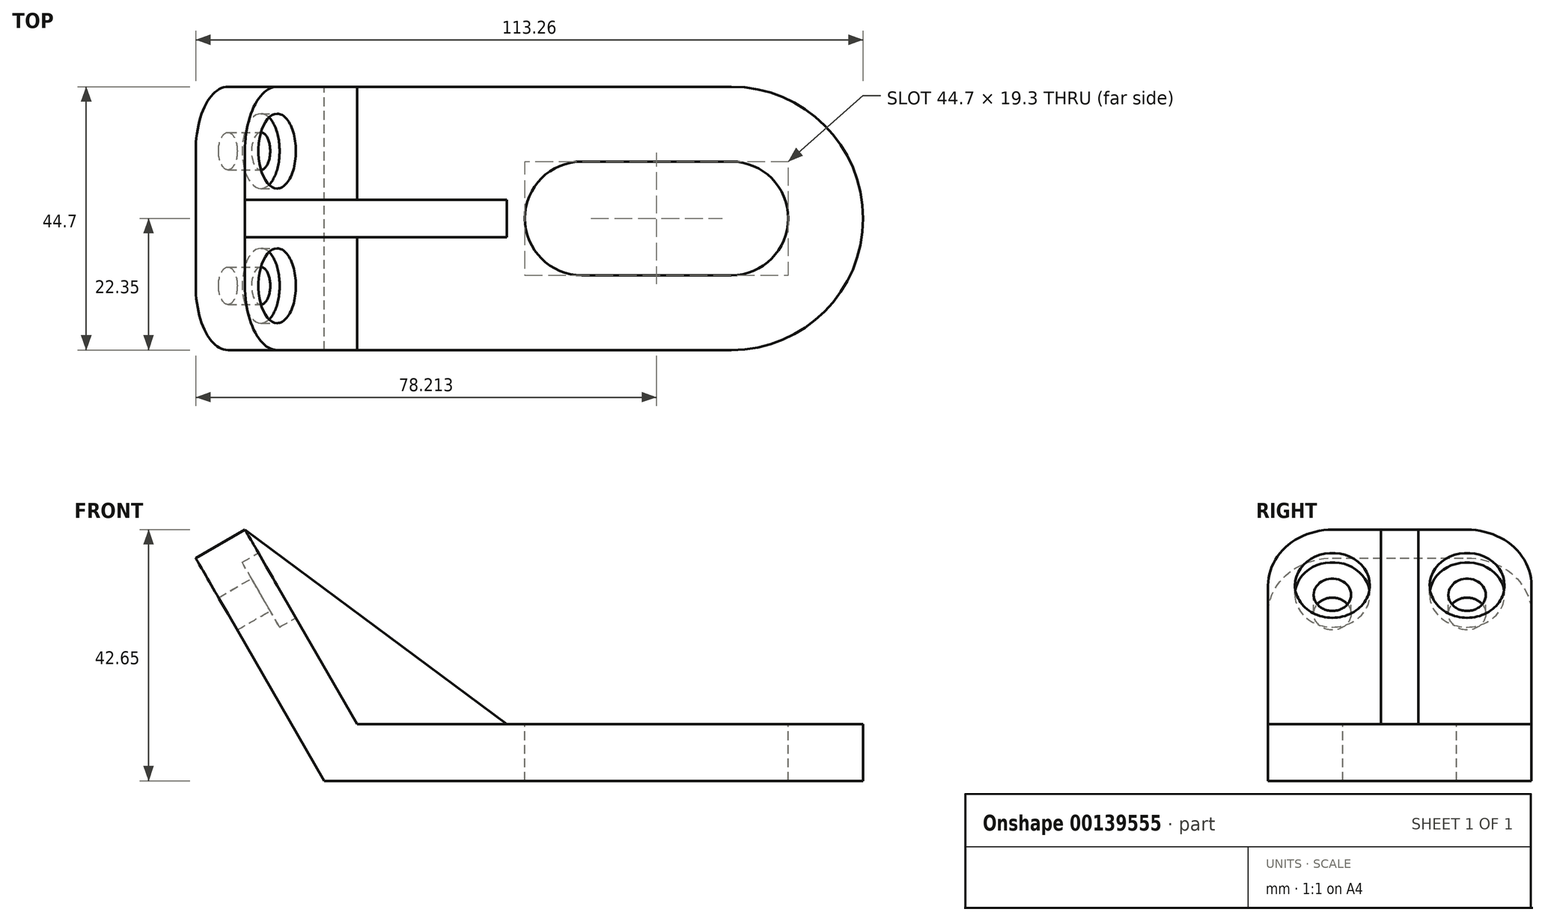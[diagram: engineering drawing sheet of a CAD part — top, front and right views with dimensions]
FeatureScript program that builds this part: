
annotation { "Feature Type Name" : "Feature", "Feature Type Description" : "" }
export const myFeature = defineFeature(function(context is Context, id is Id, definition is map)
    precondition{}
    {
        {
            var Q0;
            Q0=qCreatedBy(makeId("Front.planeOp"),FACE);
            var sketch = newSketch(context, id + "F0", { "sketchPlane" : qUnion([Q0])});
            skLineSegment(sketch, "E0", {"start": v(0, 0) * mm, "end": v(91.42, 0) * mm});
            skLineSegment(sketch, "E1", {"start": v(91.42, 0) * mm, "end": v(91.42, 9.65) * mm});
            skLineSegment(sketch, "E2", {"start": v(0, 0) * mm, "end": v(-21.84, 37.82) * mm});
            skLineSegment(sketch, "E3", {"start": v(-21.84, 37.82) * mm, "end": v(-13.48, 42.65) * mm});
            skLineSegment(sketch, "E4", {"start": v(-13.48, 42.65) * mm, "end": v(5.57, 9.65) * mm});
            skLineSegment(sketch, "E5", {"start": v(5.57, 9.65) * mm, "end": v(91.42, 9.65) * mm});
            skSolve(sketch);
        }
        {
            var Q0;
            Q0=qSketchRegion(id+"F0",true);
            extrude(context, id + "F1", {"entities" : qUnion([Q0]), "depth" : 22.35 * mm, "hasSecondDirection" : true, "secondDirectionOppositeDirection" : true, "secondDirectionDepth" : 22.35 * mm});
        }
        {
            var Q0;
            Q0=qCreatedBy(makeId("Front.planeOp"),FACE);
            var sketch = newSketch(context, id + "F2", { "sketchPlane" : qUnion([Q0])});
            skLineSegment(sketch, "E6.0", {"start": v(5.57, 9.65) * mm, "end": v(91.42, 9.65) * mm, "construction": true});
            skLineSegment(sketch, "E7.0", {"start": v(-13.48, 42.65) * mm, "end": v(5.57, 9.65) * mm, "construction": true});
            skPoint(sketch, "E8", {"position": v(30.97, 9.65) * mm});
            skLineSegment(sketch, "E9", {"start": v(-13.48, 42.65) * mm, "end": v(30.97, 9.65) * mm});
            skLineSegment(sketch, "E10", {"start": v(-13.48, 42.65) * mm, "end": v(5.57, 9.65) * mm});
            skLineSegment(sketch, "E11", {"start": v(5.57, 9.65) * mm, "end": v(30.97, 9.65) * mm});
            skSolve(sketch);
        }
        {
            var Q0;
            Q0=qSketchRegion(id+"F2",true);
            extrude(context, id + "F3", {"entities" : qUnion([Q0]), "operationType" : NewBodyOperationType.ADD, "depth" : 3.17 * mm, "hasSecondDirection" : true, "secondDirectionOppositeDirection" : true, "secondDirectionDepth" : 3.17 * mm});
        }
        {
            var Q0;
            Q0=makeQuery(id+"F1.opExtrude","CAP_EDGE",EDGE,{"disambiguationData":[OSD([sQuery(id+"F0.wireOp",EDGE,"E3")])],"isStart":false});
            var Q1;
            Q1=makeQuery(id+"F1.opExtrude","CAP_EDGE",EDGE,{"disambiguationData":[OSD([sQuery(id+"F0.wireOp",EDGE,"E3")])],"isStart":true});
            fillet(context, id + "F4", {"entities" : qUnion([Q0, Q1]), "radius" : 10.92 * mm, "tangentPropagation" : true, "allowEdgeOverflow" : false});
        }
        {
            var Q0;
            Q0=makeQuery(id+"F1.opExtrude","CAP_EDGE",EDGE,{"disambiguationData":[OSD([sQuery(id+"F0.wireOp",EDGE,"E1")])],"isStart":false});
            var Q1;
            Q1=makeQuery(id+"F1.opExtrude","CAP_EDGE",EDGE,{"disambiguationData":[OSD([sQuery(id+"F0.wireOp",EDGE,"E1")])],"isStart":true});
            fillet(context, id + "F5", {"entities" : qUnion([Q0, Q1]), "radius" : 22.35 * mm, "tangentPropagation" : true, "allowEdgeOverflow" : false});
        }
        {
            var Q0;
            Q0=makeQuery(id+"F1.opExtrude","SWEPT_FACE",FACE,{"disambiguationData":[OSD([sQuery(id+"F0.wireOp",EDGE,"E5")])]});
            var sketch = newSketch(context, id + "F6", { "sketchPlane" : qUnion([Q0])});
            skLineSegment(sketch, "E12.0", {"start": v(5.57, -22.35) * mm, "end": v(5.57, -3.18) * mm});
            skPoint(sketch, "E13", {"position": v(43.67, 0) * mm});
            skPoint(sketch, "E14", {"position": v(69.07, 0) * mm});
            skArc(sketch, "E15", {"start": v(69.07, -9.65) * mm, "mid": v(78.72, 0) * mm, "end": v(69.07, 9.65) * mm});
            skArc(sketch, "E16", {"start": v(43.67, 9.65) * mm, "mid": v(34.02, 0) * mm, "end": v(43.67, -9.65) * mm});
            skLineSegment(sketch, "E17", {"start": v(43.67, 9.65) * mm, "end": v(69.07, 9.65) * mm});
            skLineSegment(sketch, "E18", {"start": v(43.67, -9.65) * mm, "end": v(69.07, -9.65) * mm});
            skArc(sketch, "E19.0", {"start": v(69.07, -22.35) * mm, "mid": v(91.42, 0) * mm, "end": v(69.07, 22.35) * mm});
            skSolve(sketch);
        }
        {
            var Q0;
            Q0=qSketchRegion(id+"F6",true);
            var Q1;
            Q1=makeQuery(id+"F1.opExtrude","SWEPT_FACE",FACE,{"disambiguationData":[OSD([sQuery(id+"F0.wireOp",EDGE,"E0")])]});
            extrude(context, id + "F7", {"entities" : qUnion([Q0]), "operationType" : NewBodyOperationType.REMOVE, "endBound" : BoundingType.UP_TO_SURFACE, "oppositeDirection" : true, "endBoundEntityFace" : qUnion([Q1]), "depth" : 25.4 * mm});
        }
        {
            var Q0;
            {var subQ0=sQuery(id+"F2.wireOp",EDGE,"E9");var subQ3=sQuery(id+"F0.wireOp",EDGE,"E4");Q0=makeQuery(id+"F3.boolean.opBoolean","SPLIT",FACE,{"disambiguationData":[TD([makeQuery(id+"F3.opExtrude","CAP_FACE",FACE,{"disambiguationData":[OSD([subQ0,sQuery(id+"F2.wireOp",EDGE,"E10"),sQuery(id+"F2.wireOp",EDGE,"E11")])],"isStart":false})])],"derivedFrom":makeQuery(id+"F1.opExtrude","SWEPT_FACE",FACE,{"disambiguationData":[OSD([subQ3])]})});}
            var sketch = newSketch(context, id + "F8", { "sketchPlane" : qUnion([Q0])});
            skLineSegment(sketch, "E20.0", {"start": v(-11.43, 43.67) * mm, "end": v(-3.18, 43.67) * mm});
            skLineSegment(sketch, "E21.0", {"start": v(-22.35, 5.57) * mm, "end": v(-3.18, 5.57) * mm});
            skSolve(sketch);
        }
        {
            var Q0;
            Q0=makeQuery(id+"F8.imprint","IMPRINT",FACE,{"disambiguationData":[TD([[makeQuery(id+"F8.imprint","IMPRINT",EDGE,{"derivedFrom":sQuery(id+"F8.wireOp",EDGE,"E20.0")}),-1.0]])]});
            var sketch = newSketch(context, id + "F9", { "sketchPlane" : qUnion([Q0])});
            skLineSegment(sketch, "E22.0", {"start": v(-11.43, 43.67) * mm, "end": v(-3.18, 43.67) * mm, "construction": true});
            skLineSegment(sketch, "E23.0", {"start": v(-22.35, 5.57) * mm, "end": v(-3.18, 5.57) * mm});
            skArc(sketch, "E24.0", {"start": v(-11.43, 43.67) * mm, "mid": v(-19.15, 40.47) * mm, "end": v(-22.35, 32.75) * mm, "construction": true});
            skCircle(sketch, "E25", {"center": v(-11.43, 32.75) * mm, "radius": 3.18 * mm});
            skCircle(sketch, "E26", {"center": v(-11.43, 32.75) * mm, "radius": 6.35 * mm});
            skSolve(sketch);
        }
        {
            var Q0;
            Q0=makeQuery(id+"F9.imprint","IMPRINT",FACE,{"disambiguationData":[TD([[makeQuery(id+"F9.imprint","IMPRINT",EDGE,{"derivedFrom":sQuery(id+"F9.wireOp",EDGE,"E25")}),-1.0]])]});
            var Q1;
            Q1=makeQuery(id+"F9.imprint","IMPRINT",FACE,{"disambiguationData":[TD([[makeQuery(id+"F9.imprint","IMPRINT",EDGE,{"derivedFrom":sQuery(id+"F9.wireOp",EDGE,"E25")}),1.0]])]});
            extrude(context, id + "F10", {"entities" : qUnion([Q0, Q1]), "operationType" : NewBodyOperationType.REMOVE, "oppositeDirection" : true, "depth" : 3.17 * mm});
        }
        {
            var Q0;
            Q0=makeQuery(id+"F9.imprint","IMPRINT",FACE,{"disambiguationData":[TD([[makeQuery(id+"F9.imprint","IMPRINT",EDGE,{"derivedFrom":sQuery(id+"F9.wireOp",EDGE,"E25")}),1.0]])]});
            extrude(context, id + "F11", {"entities" : qUnion([Q0]), "operationType" : NewBodyOperationType.REMOVE, "endBound" : BoundingType.THROUGH_ALL, "oppositeDirection" : true, "depth" : 25.4 * mm});
        }
        {
            var Q0;
            {var subQ2=sQuery(id+"F2.wireOp",EDGE,"E9");var subQ3=sQuery(id+"F0.wireOp",EDGE,"E4");Q0=makeQuery(id+"F3.boolean.opBoolean","SPLIT",FACE,{"disambiguationData":[TD([makeQuery(id+"F3.opExtrude","CAP_FACE",FACE,{"disambiguationData":[OSD([subQ2,sQuery(id+"F2.wireOp",EDGE,"E10"),sQuery(id+"F2.wireOp",EDGE,"E11")])],"isStart":true})])],"derivedFrom":makeQuery(id+"F1.opExtrude","SWEPT_FACE",FACE,{"disambiguationData":[OSD([subQ3])]})});}
            var sketch = newSketch(context, id + "F12", { "sketchPlane" : qUnion([Q0])});
            skArc(sketch, "E27.0", {"start": v(22.35, 32.75) * mm, "mid": v(19.15, 40.47) * mm, "end": v(11.43, 43.67) * mm});
            skCircle(sketch, "E28", {"center": v(11.43, 32.75) * mm, "radius": 6.35 * mm});
            skCircle(sketch, "E29", {"center": v(11.43, 32.75) * mm, "radius": 3.18 * mm});
            skSolve(sketch);
        }
        {
            var Q0;
            Q0=qSketchRegion(id+"F12",true);
            var Q1;
            Q1=makeQuery(id+"F12.imprint","IMPRINT",FACE,{"disambiguationData":[TD([[makeQuery(id+"F12.imprint","IMPRINT",EDGE,{"derivedFrom":sQuery(id+"F12.wireOp",EDGE,"E29")}),1.0]])]});
            extrude(context, id + "F13", {"entities" : qUnion([Q0, Q1]), "operationType" : NewBodyOperationType.REMOVE, "oppositeDirection" : true, "depth" : 3.19 * mm});
        }
        {
            var Q0;
            Q0=makeQuery(id+"F12.imprint","IMPRINT",FACE,{"disambiguationData":[TD([[makeQuery(id+"F12.imprint","IMPRINT",EDGE,{"derivedFrom":sQuery(id+"F12.wireOp",EDGE,"E29")}),1.0]])]});
            extrude(context, id + "F14", {"entities" : qUnion([Q0]), "operationType" : NewBodyOperationType.REMOVE, "endBound" : BoundingType.THROUGH_ALL, "oppositeDirection" : true, "depth" : 25.4 * mm});
        }
    });
